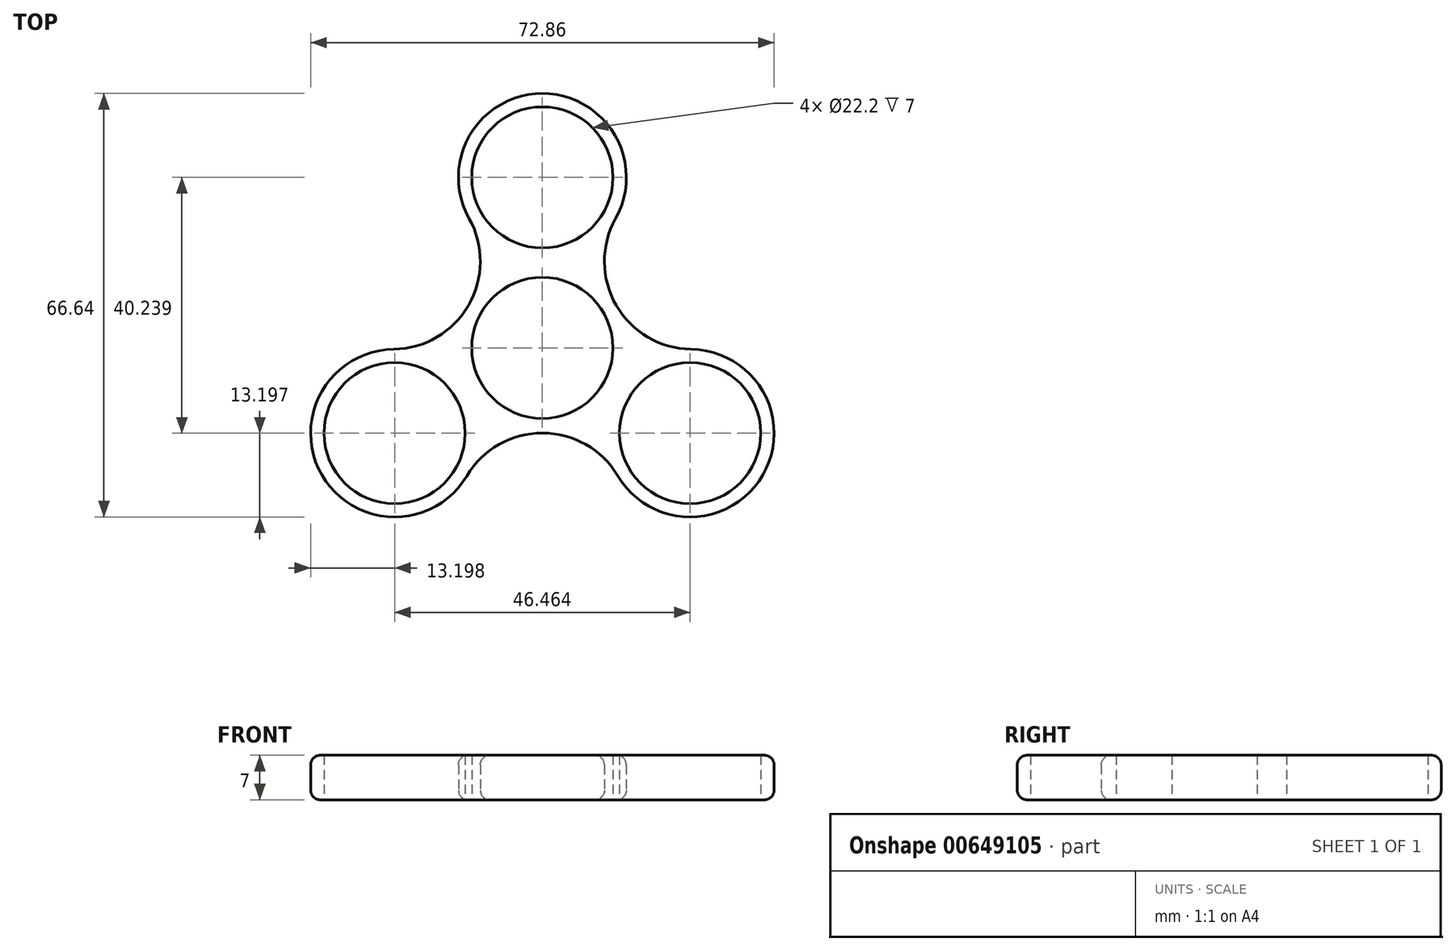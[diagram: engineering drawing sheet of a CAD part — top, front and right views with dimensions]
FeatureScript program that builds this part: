
annotation { "Feature Type Name" : "Feature", "Feature Type Description" : "" }
export const myFeature = defineFeature(function(context is Context, id is Id, definition is map)
    precondition{}
    {
        {
            var Q0;
            Q0=qCreatedBy(makeId("Top.planeOp"),FACE);
            var sketch = newSketch(context, id + "F0", { "sketchPlane" : qUnion([Q0])});
            skCircle(sketch, "E0", {"center": v(0, 0) * mm, "radius": 11.1 * mm});
            skCircle(sketch, "E1", {"center": v(0, 26.83) * mm, "radius": 11.1 * mm});
            skArc(sketch, "E2", {"start": v(11.5, 20.33) * mm, "mid": v(0, 40.03) * mm, "end": v(-11.5, 20.33) * mm});
            skArc(sketch, "E3.1.0", {"start": v(-23.35, -0.21) * mm, "mid": v(-34.66, -20.01) * mm, "end": v(-11.86, -20.12) * mm});
            skCircle(sketch, "E3.1.1", {"center": v(-23.23, -13.41) * mm, "radius": 11.1 * mm});
            skArc(sketch, "E3.2.0", {"start": v(11.86, -20.12) * mm, "mid": v(34.66, -20.01) * mm, "end": v(23.35, -0.21) * mm});
            skCircle(sketch, "E3.2.1", {"center": v(23.23, -13.41) * mm, "radius": 11.1 * mm});
            skLineSegment(sketch, "E4", {"start": v(-11.61, 6.7) * mm, "end": v(-11.62, 6.7) * mm, "construction": true});
            skArc(sketch, "E5", {"start": v(-23.35, -0.21) * mm, "mid": v(-11.61, 6.7) * mm, "end": v(-11.5, 20.33) * mm});
            skArc(sketch, "E6.1.0", {"start": v(11.86, -20.12) * mm, "mid": v(0, -13.4) * mm, "end": v(-11.86, -20.12) * mm});
            skArc(sketch, "E6.2.0", {"start": v(11.5, 20.33) * mm, "mid": v(11.61, 6.7) * mm, "end": v(23.35, -0.21) * mm});
            skLineSegment(sketch, "E7.trimOffspring", {"start": v(-23.48, 13.56) * mm, "end": v(-23.6, 13.62) * mm, "construction": true});
            skLineSegment(sketch, "E8.trimOffspring", {"start": v(-11.82, 6.36) * mm, "end": v(-11.42, 7.05) * mm, "construction": true});
            skSolve(sketch);
        }
        {
            var Q0;
            Q0=makeQuery(id+"F0.imprint","IMPRINT",FACE,{"disambiguationData":[TD([[makeQuery(id+"F0.imprint","IMPRINT",EDGE,{"derivedFrom":sQuery(id+"F0.wireOp",EDGE,"E0")}),-1.0]])]});
            extrude(context, id + "F1", {"entities" : qUnion([Q0]), "depth" : 7 * mm, "offsetDistance" : 25 * mm});
        }
        {
            var Q0;
            Q0=makeQuery(id+"F1.opExtrude","CAP_EDGE",EDGE,{"disambiguationData":[OSD([sQuery(id+"F0.wireOp",EDGE,"E6.1.0")])],"isStart":false});
            var Q1;
            Q1=makeQuery(id+"F1.opExtrude","CAP_EDGE",EDGE,{"disambiguationData":[OSD([sQuery(id+"F0.wireOp",EDGE,"E3.1.0")])],"isStart":false});
            var Q2;
            Q2=makeQuery(id+"F1.opExtrude","CAP_EDGE",EDGE,{"disambiguationData":[OSD([sQuery(id+"F0.wireOp",EDGE,"E5")])],"isStart":false});
            var Q3;
            Q3=makeQuery(id+"F1.opExtrude","CAP_EDGE",EDGE,{"disambiguationData":[OSD([sQuery(id+"F0.wireOp",EDGE,"E2")])],"isStart":false});
            var Q4;
            Q4=makeQuery(id+"F1.opExtrude","CAP_EDGE",EDGE,{"disambiguationData":[OSD([sQuery(id+"F0.wireOp",EDGE,"E6.2.0")])],"isStart":false});
            var Q5;
            Q5=makeQuery(id+"F1.opExtrude","CAP_EDGE",EDGE,{"disambiguationData":[OSD([sQuery(id+"F0.wireOp",EDGE,"E3.2.0")])],"isStart":false});
            fillet(context, id + "F2", {"entities" : qUnion([Q0, Q1, Q2, Q3, Q4, Q5]), "radius" : 1.5 * mm, "tangentPropagation" : true, "allowEdgeOverflow" : false});
        }
        {
            var Q0;
            Q0=makeQuery(id+"F1.opExtrude","CAP_EDGE",EDGE,{"disambiguationData":[OSD([sQuery(id+"F0.wireOp",EDGE,"E6.2.0")])],"isStart":true});
            var Q1;
            Q1=makeQuery(id+"F1.opExtrude","CAP_EDGE",EDGE,{"disambiguationData":[OSD([sQuery(id+"F0.wireOp",EDGE,"E2")])],"isStart":true});
            var Q2;
            Q2=makeQuery(id+"F1.opExtrude","CAP_EDGE",EDGE,{"disambiguationData":[OSD([sQuery(id+"F0.wireOp",EDGE,"E3.2.0")])],"isStart":true});
            var Q3;
            Q3=makeQuery(id+"F1.opExtrude","CAP_EDGE",EDGE,{"disambiguationData":[OSD([sQuery(id+"F0.wireOp",EDGE,"E6.1.0")])],"isStart":true});
            var Q4;
            Q4=makeQuery(id+"F1.opExtrude","CAP_EDGE",EDGE,{"disambiguationData":[OSD([sQuery(id+"F0.wireOp",EDGE,"E3.1.0")])],"isStart":true});
            fillet(context, id + "F3", {"entities" : qUnion([Q0, Q1, Q2, Q3, Q4]), "radius" : 1.5 * mm, "tangentPropagation" : true, "allowEdgeOverflow" : false});
        }
    });
